# Revit family: 2871T1-V3
name_source: partatom
category: Plumbing Fixtures
revit_build: Autodesk Revit 2015 (Build: 20140606_1530(x64)
units: mm (PartAtom-declared; Revit-internal decimal feet)

## types (1)
- 2871T1-V3
    Category = Sink mixer
    DLB090017 = Brass, Chrome plated
    Default Elevation = 1219 mm
    Description = French manufacturer Delabie is a leader in the European sanitary ware market for non-domestic places. Water controls, solutions for disabled people, sanitary ware, for schools, leisure centres, offices, hospitals, airports…
    Diameter = 15 mm  [stored 0.0492126 ft]
    Features = Deck-mounted mechanical sink mixer without pop-up waste.  High, swivelling, removable BIOCLIP spout H. 160mm supplied with 1 disposable, recyclable Hostaform® spout L. 175mm, Ø 22mm with star-shaped flow straightener.  Ø 40mm ceramic cartridge. Pre-set maximum temperature limiter. Body and spout with smooth interiors. Flow rate limited to 5 lpm at 3 bar. Hygiene control lever L. 215mm requires no manual contact.  Chrome-plated brass body and base.  Reinforced fixing via 2 stainless steel rods. PEX F3/8".
    Finish = Chrome-plated
    FlowRate = 5 lpm
    Grade = ACS, PZH
    IntegralAccessories = PEX flexibles
    IntegralAccessoryOptions = Wastes
    Manufacturer = DELABIE
    ManufacturerName = DELABIE
    Material = Brass
    Model = Mechanical sink mixer H.160mm L.175mm
    Model number = 2871T1
    Name = 2871T1
    NominalHeight = 16 cm
    NominalWidth = 17,5 cm
    Operation = Mechanical mixer
    Polantis code = DLB090017
    ProductInformation = http://www.delabie.com
    SerialNumber = 3456330119818
    URL = http://www.delabie.com
    WarrantyDescription = Any manufacturing defect
    WarrantyDurationUnit = 10 years
    WaterSupplyTemperatureMaximum = 55°C-85° (∆50°C : CW/HW)

note: [stored X ft] marks values corroborated as IEEE doubles in the binary element streams (Revit-internal decimal feet)

## geometry (parser evidence)
native form markers: Sweep x6
no freeform markers — native parametric forms only
